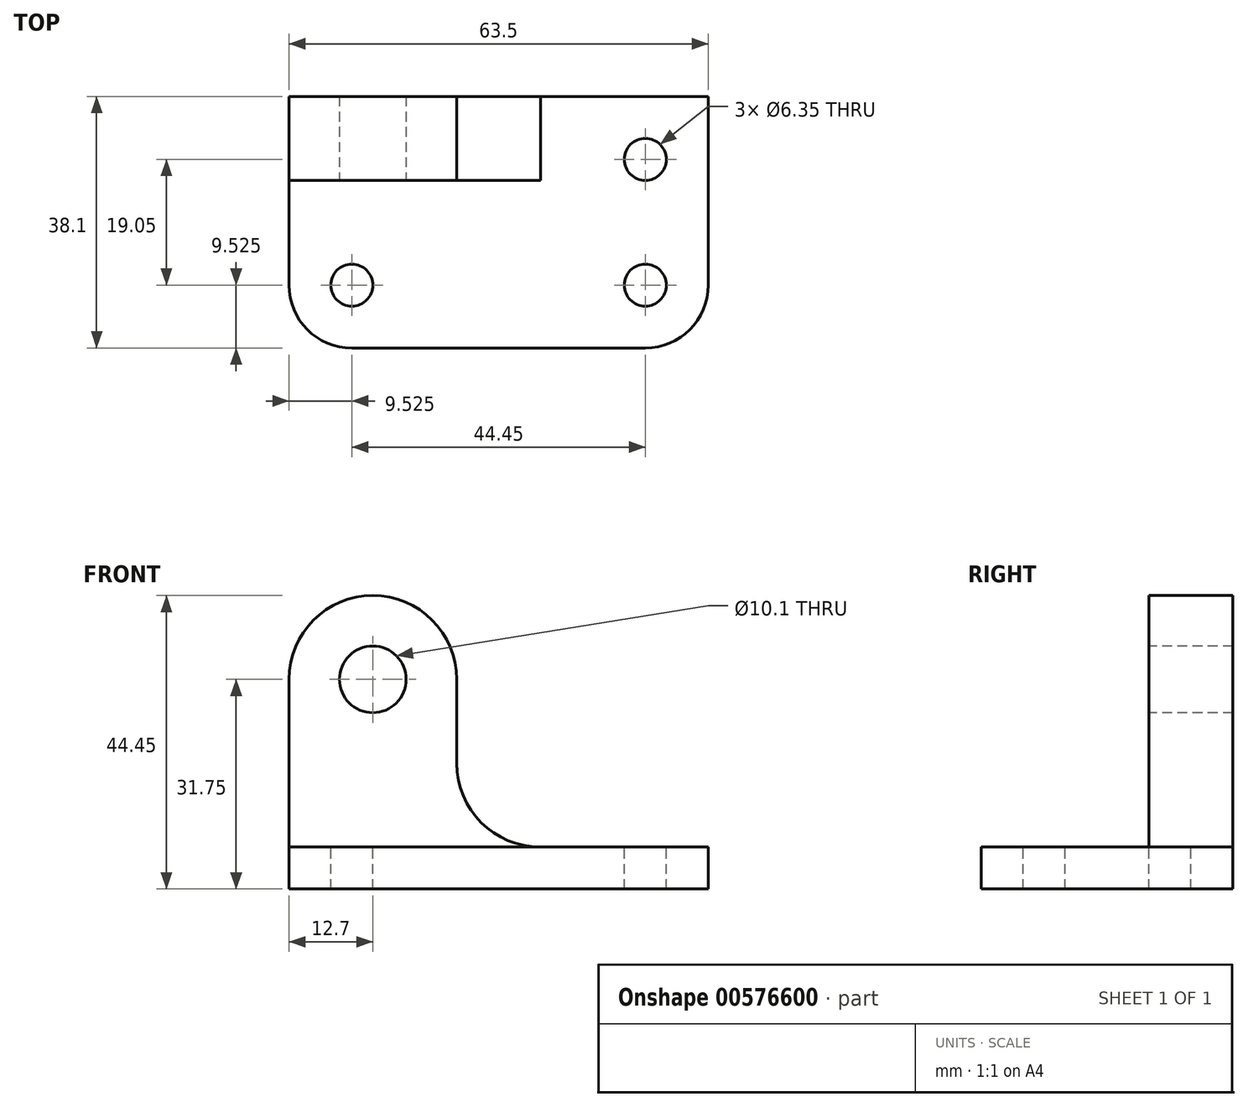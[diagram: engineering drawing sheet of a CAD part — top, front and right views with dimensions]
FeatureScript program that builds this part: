
annotation { "Feature Type Name" : "Feature", "Feature Type Description" : "" }
export const myFeature = defineFeature(function(context is Context, id is Id, definition is map)
    precondition{}
    {
        {
            var Q0;
            Q0=qCreatedBy(makeId("Top.planeOp"),FACE);
            var sketch = newSketch(context, id + "F0", { "sketchPlane" : qUnion([Q0])});
            skLineSegment(sketch, "E0", {"start": v(0, 0) * mm, "end": v(63.5, 0) * mm});
            skLineSegment(sketch, "E1", {"start": v(63.5, 0) * mm, "end": v(63.5, 38.1) * mm});
            skLineSegment(sketch, "E2", {"start": v(63.5, 38.1) * mm, "end": v(0, 38.1) * mm});
            skLineSegment(sketch, "E3", {"start": v(0, 38.1) * mm, "end": v(0, 0) * mm});
            skSolve(sketch);
        }
        {
            var Q0;
            Q0=makeQuery(id+"F0.imprint","IMPRINT",FACE,{"disambiguationData":[TD([[makeQuery(id+"F0.imprint","IMPRINT",EDGE,{"derivedFrom":sQuery(id+"F0.wireOp",EDGE,"E0")}),1.0]])]});
            extrude(context, id + "F1", {"entities" : qUnion([Q0]), "depth" : 6.35 * mm, "offsetDistance" : 25.4 * mm});
        }
        {
            var Q0;
            Q0=makeQuery(id+"F1.opExtrude","CAP_FACE",FACE,{"disambiguationData":[OSD([sQuery(id+"F0.wireOp",EDGE,"E0"),sQuery(id+"F0.wireOp",EDGE,"E1"),sQuery(id+"F0.wireOp",EDGE,"E2"),sQuery(id+"F0.wireOp",EDGE,"E3")])],"isStart":false});
            var sketch = newSketch(context, id + "F2", { "sketchPlane" : qUnion([Q0])});
            skCircle(sketch, "E4", {"center": v(9.53, 9.53) * mm, "radius": 3.18 * mm});
            skCircle(sketch, "E5", {"center": v(53.98, 9.53) * mm, "radius": 3.18 * mm});
            skCircle(sketch, "E6", {"center": v(53.98, 28.58) * mm, "radius": 3.18 * mm});
            skArc(sketch, "E7", {"start": v(0, 9.52) * mm, "mid": v(2.79, 2.79) * mm, "end": v(9.52, 0) * mm});
            skPoint(sketch, "E8.center.orphan", {"position": v(61, 2.5) * mm});
            skPoint(sketch, "E8.end.orphan", {"position": v(63.5, 9.52) * mm});
            skPoint(sketch, "E8.start.orphan", {"position": v(53.98, 0) * mm});
            skArc(sketch, "E9", {"start": v(53.98, 0) * mm, "mid": v(60.71, 2.79) * mm, "end": v(63.5, 9.52) * mm});
            skSolve(sketch);
        }
        {
            var Q0;
            Q0=makeQuery(id+"F2.imprint","IMPRINT",FACE,{"disambiguationData":[TD([[makeQuery(id+"F2.imprint","IMPRINT",EDGE,{"derivedFrom":sQuery(id+"F2.wireOp",EDGE,"E6")}),1.0]])]});
            var Q1;
            Q1=makeQuery(id+"F2.imprint","IMPRINT",FACE,{"disambiguationData":[TD([[makeQuery(id+"F2.imprint","IMPRINT",EDGE,{"derivedFrom":sQuery(id+"F2.wireOp",EDGE,"E5")}),1.0]])]});
            var Q2;
            Q2=makeQuery(id+"F2.imprint","IMPRINT",FACE,{"disambiguationData":[TD([[makeQuery(id+"F2.imprint","IMPRINT",EDGE,{"derivedFrom":sQuery(id+"F2.wireOp",EDGE,"E4")}),1.0]])]});
            var Q3;
            {var subQ0=sQuery(id+"F2.wireOp",EDGE,"E7");Q3=makeQuery(id+"F2.imprint","IMPRINT",FACE,{"disambiguationData":[TD([[makeQuery(id+"F2.imprint","IMPRINT",EDGE,{"derivedFrom":subQ0}),-1.0]])]});}
            var Q4;
            {var subQ0=sQuery(id+"F2.wireOp",EDGE,"E9");Q4=makeQuery(id+"F2.imprint","IMPRINT",FACE,{"disambiguationData":[TD([[makeQuery(id+"F2.imprint","IMPRINT",EDGE,{"derivedFrom":subQ0}),-1.0]])]});}
            extrude(context, id + "F3", {"entities" : qUnion([Q0, Q1, Q2, Q3, Q4]), "operationType" : NewBodyOperationType.REMOVE, "oppositeDirection" : true, "depth" : 25.4 * mm, "offsetDistance" : 25.4 * mm});
        }
        {
            var Q0;
            Q0=makeQuery(id+"F1.opExtrude","SWEPT_FACE",FACE,{"disambiguationData":[OSD([sQuery(id+"F0.wireOp",EDGE,"E2")])]});
            var sketch = newSketch(context, id + "F4", { "sketchPlane" : qUnion([Q0])});
            skLineSegment(sketch, "E10", {"start": v(0, 6.35) * mm, "end": v(0, 44.45) * mm});
            skLineSegment(sketch, "E11", {"start": v(0, 44.45) * mm, "end": v(-38.1, 44.45) * mm});
            skLineSegment(sketch, "E12", {"start": v(-38.1, 44.45) * mm, "end": v(-38.1, 6.35) * mm});
            skSolve(sketch);
        }
        {
            var Q0;
            {var subQ0=sQuery(id+"F4.wireOp",EDGE,"E10");Q0=makeQuery(id+"F4.imprint","IMPRINT",FACE,{"disambiguationData":[TD([[makeQuery(id+"F4.imprint","IMPRINT",EDGE,{"derivedFrom":subQ0}),1.0]])]});}
            extrude(context, id + "F5", {"entities" : qUnion([Q0]), "oppositeDirection" : true, "depth" : 12.7 * mm, "offsetDistance" : 25.4 * mm});
        }
        {
            var Q0;
            Q0=makeQuery(id+"F5.opExtrude","CAP_FACE",FACE,{"disambiguationData":[OSD([sQuery(id+"F0.wireOp",EDGE,"E2"),sQuery(id+"F4.wireOp",EDGE,"E10"),sQuery(id+"F4.wireOp",EDGE,"E11"),sQuery(id+"F4.wireOp",EDGE,"E12")])],"isStart":false});
            var sketch = newSketch(context, id + "F6", { "sketchPlane" : qUnion([Q0])});
            skCircle(sketch, "E13", {"center": v(12.7, 31.75) * mm, "radius": 5.05 * mm});
            skArc(sketch, "E14", {"start": v(12.7, 44.45) * mm, "mid": v(3.72, 40.73) * mm, "end": v(0, 31.75) * mm});
            skArc(sketch, "E15", {"start": v(25.4, 31.75) * mm, "mid": v(21.68, 40.73) * mm, "end": v(12.7, 44.45) * mm});
            skLineSegment(sketch, "E16", {"start": v(25.4, 31.75) * mm, "end": v(25.4, 19.05) * mm});
            skArc(sketch, "E17", {"start": v(25.4, 19.05) * mm, "mid": v(29.12, 10.07) * mm, "end": v(38.1, 6.35) * mm});
            skSolve(sketch);
        }
        {
            var Q0;
            {var subQ1=sQuery(id+"F6.wireOp",EDGE,"E15");Q0=makeQuery(id+"F6.imprint","IMPRINT",FACE,{"disambiguationData":[TD([[makeQuery(id+"F6.imprint","IMPRINT",EDGE,{"derivedFrom":subQ1}),-1.0]])]});}
            var Q1;
            {var subQ0=sQuery(id+"F6.wireOp",EDGE,"E14");Q1=makeQuery(id+"F6.imprint","IMPRINT",FACE,{"disambiguationData":[TD([[makeQuery(id+"F6.imprint","IMPRINT",EDGE,{"derivedFrom":subQ0}),-1.0]])]});}
            var Q2;
            Q2=makeQuery(id+"F6.imprint","IMPRINT",FACE,{"disambiguationData":[TD([[makeQuery(id+"F6.imprint","IMPRINT",EDGE,{"derivedFrom":sQuery(id+"F6.wireOp",EDGE,"E13")}),1.0]])]});
            extrude(context, id + "F7", {"entities" : qUnion([Q0, Q1, Q2]), "operationType" : NewBodyOperationType.REMOVE, "oppositeDirection" : true, "depth" : 25.4 * mm, "offsetDistance" : 25.4 * mm});
        }
    });
